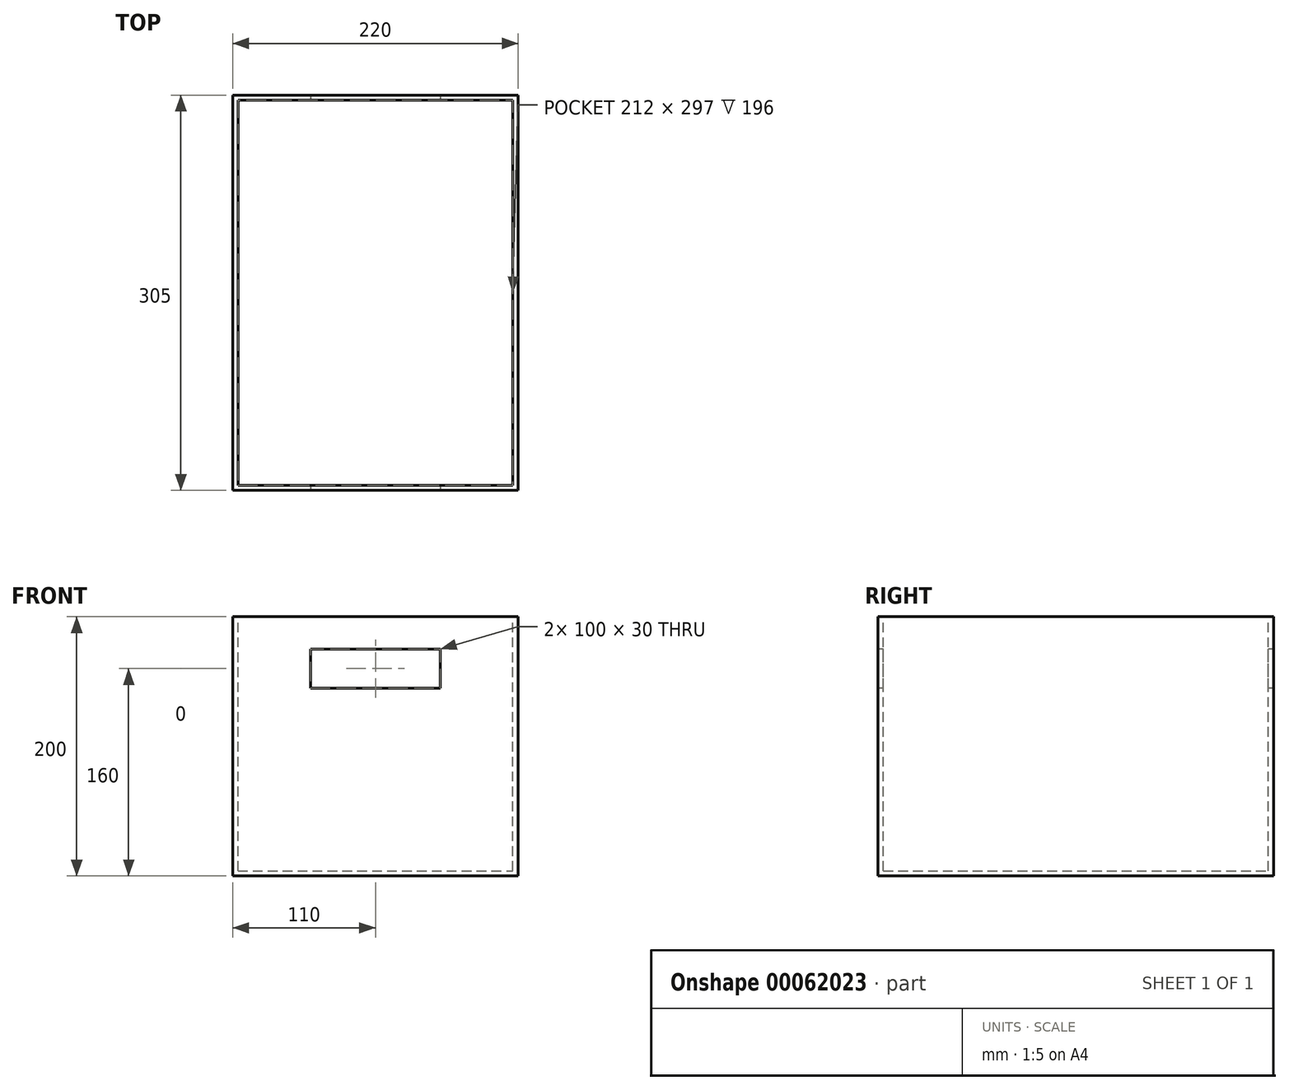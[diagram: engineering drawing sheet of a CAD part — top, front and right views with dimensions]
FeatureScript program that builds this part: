
annotation { "Feature Type Name" : "Feature", "Feature Type Description" : "" }
export const myFeature = defineFeature(function(context is Context, id is Id, definition is map)
    precondition{}
    {
        {
            var Q0;
            Q0=qCreatedBy(makeId("Front.planeOp"),FACE);
            var sketch = newSketch(context, id + "F0", { "sketchPlane" : qUnion([Q0])});
            skLineSegment(sketch, "E0.bottom", {"start": v(0, 0) * mm, "end": v(220, 0) * mm});
            skLineSegment(sketch, "E0.top", {"start": v(0, 200) * mm, "end": v(220, 200) * mm});
            skLineSegment(sketch, "E0.left", {"start": v(0, 0) * mm, "end": v(0, 200) * mm});
            skLineSegment(sketch, "E0.right", {"start": v(220, 0) * mm, "end": v(220, 200) * mm});
            skSolve(sketch);
        }
        {
            var Q0;
            Q0 = qSketchRegion(id + "F0", true);
            extrude(context, id + "F1", {"entities" : qUnion([Q0]), "depth" : 305 * mm});
        }
        {
            var Q0;
            Q0=makeQuery(id+"F1.opExtrude","SWEPT_FACE",FACE,{"disambiguationData":[OSD([sQuery(id+"F0.wireOp",EDGE,"E0.top")])]});
            shell(context, id + "F2", {"entities" : qUnion([Q0]), "thickness" : 4 * mm});
        }
        {
            var Q0;
            Q0=makeQuery(id+"F1.opExtrude","CAP_FACE",FACE,{"disambiguationData":[OSD([sQuery(id+"F0.wireOp",EDGE,"E0.bottom"),sQuery(id+"F0.wireOp",EDGE,"E0.top"),sQuery(id+"F0.wireOp",EDGE,"E0.left"),sQuery(id+"F0.wireOp",EDGE,"E0.right")])],"isStart":false});
            var sketch = newSketch(context, id + "F3", { "sketchPlane" : qUnion([Q0])});
            skLineSegment(sketch, "E1", {"start": v(110, 200) * mm, "end": v(110, 0) * mm, "construction": true});
            skLineSegment(sketch, "E2.rect.bottom", {"start": v(60, 145) * mm, "end": v(160, 145) * mm});
            skLineSegment(sketch, "E2.rect.top", {"start": v(60, 175) * mm, "end": v(160, 175) * mm});
            skLineSegment(sketch, "E2.rect.left", {"start": v(60, 145) * mm, "end": v(60, 175) * mm});
            skLineSegment(sketch, "E2.rect.right", {"start": v(160, 145) * mm, "end": v(160, 175) * mm});
            skPoint(sketch, "E2.rect.middle", {"position": v(110, 160) * mm});
            skSolve(sketch);
        }
        {
            var Q0;
            Q0 = qSketchRegion(id + "F3", true);
            extrude(context, id + "F4", {"entities" : qUnion([Q0]), "operationType" : NewBodyOperationType.REMOVE, "endBound" : BoundingType.THROUGH_ALL, "oppositeDirection" : true, "depth" : 25 * mm});
        }
    });
